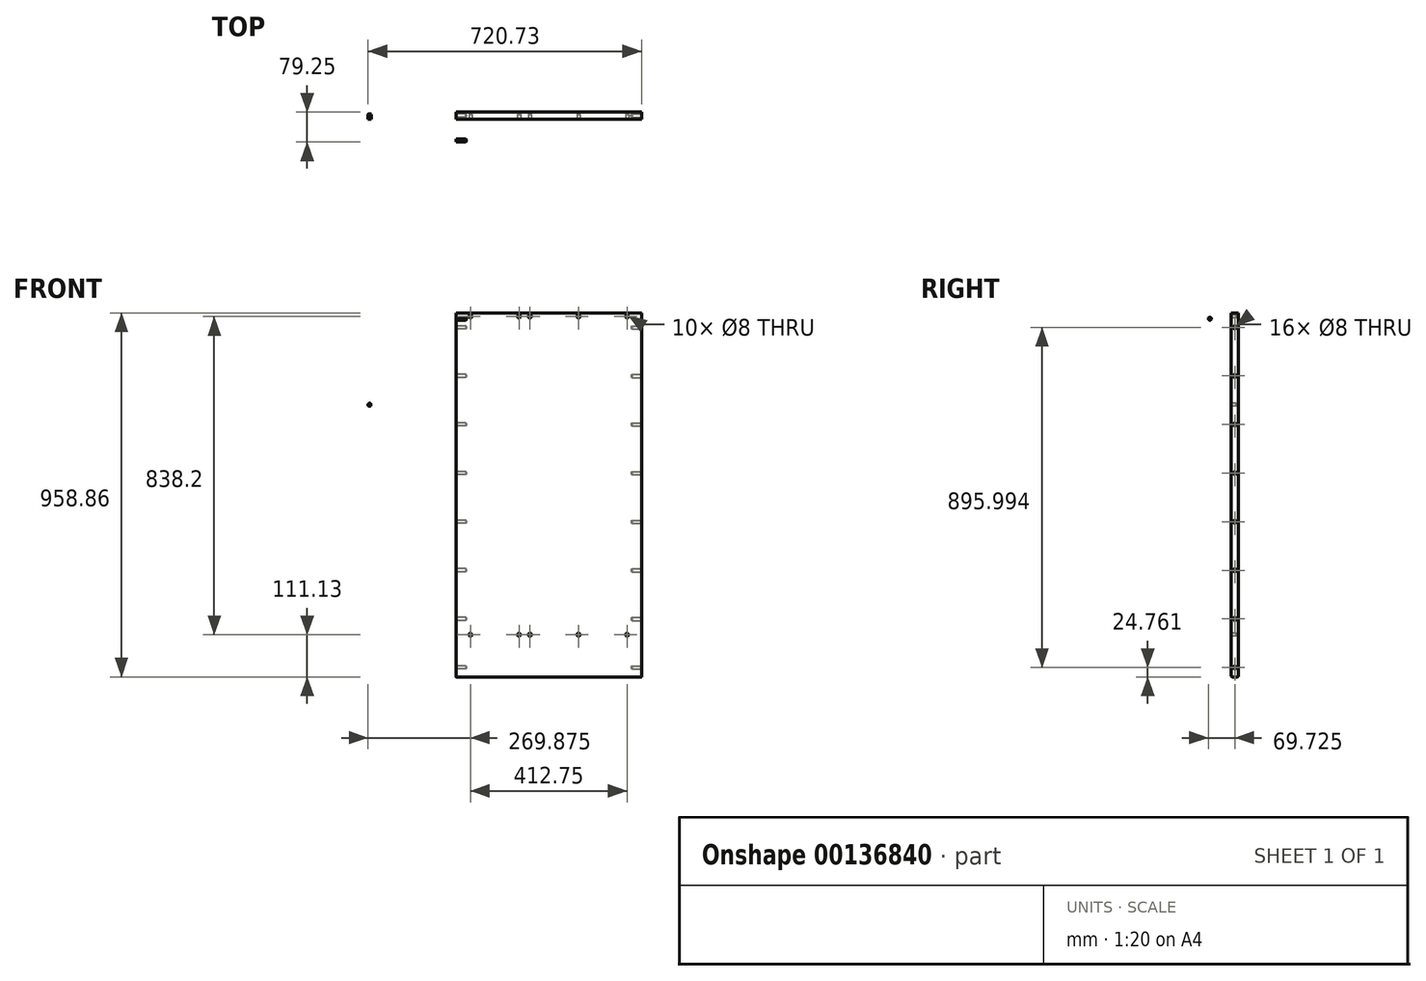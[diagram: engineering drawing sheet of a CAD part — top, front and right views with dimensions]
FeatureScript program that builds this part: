
annotation { "Feature Type Name" : "Feature", "Feature Type Description" : "" }
export const myFeature = defineFeature(function(context is Context, id is Id, definition is map)
    precondition{}
    {
        {
            var Q0;
            Q0=qCreatedBy(makeId("Front.planeOp"),FACE);
            var sketch = newSketch(context, id + "F0", { "sketchPlane" : qUnion([Q0])});
            skLineSegment(sketch, "E0.bottom", {"start": v(244.48, -479.43) * mm, "end": v(-244.47, -479.43) * mm});
            skLineSegment(sketch, "E0.top", {"start": v(244.47, 479.43) * mm, "end": v(-244.48, 479.43) * mm});
            skLineSegment(sketch, "E0.left", {"start": v(244.48, -479.43) * mm, "end": v(244.47, 479.42) * mm});
            skLineSegment(sketch, "E0.right", {"start": v(-244.47, -479.43) * mm, "end": v(-244.48, 479.43) * mm});
            skSolve(sketch);
        }
        {
            var Q0;
            Q0=makeQuery(id+"F0.imprint","IMPRINT",FACE,{"disambiguationData":[TD([[makeQuery(id+"F0.imprint","IMPRINT",EDGE,{"derivedFrom":sQuery(id+"F0.wireOp",EDGE,"E0.bottom")}),-1.0]])]});
            extrude(context, id + "F1", {"entities" : qUnion([Q0]), "oppositeDirection" : true, "depth" : 19.05 * mm});
        }
        {
            var Q0;
            Q0=makeQuery(id+"F1.opExtrude","SWEPT_FACE",FACE,{"disambiguationData":[OSD([sQuery(id+"F0.wireOp",EDGE,"E0.right")])]});
            var sketch = newSketch(context, id + "F2", { "sketchPlane" : qUnion([Q0])});
            skPoint(sketch, "E1", {"position": v(-9.53, 441.32) * mm});
            skPoint(sketch, "E2", {"position": v(-9.53, 313.32) * mm});
            skPoint(sketch, "E3", {"position": v(-9.52, 185.33) * mm});
            skPoint(sketch, "E4", {"position": v(-9.52, 57.33) * mm});
            skPoint(sketch, "E5", {"position": v(-9.52, -70.67) * mm});
            skPoint(sketch, "E6", {"position": v(-9.52, -198.67) * mm});
            skPoint(sketch, "E7", {"position": v(-9.52, -326.67) * mm});
            skPoint(sketch, "E8", {"position": v(-9.52, -454.67) * mm});
            skSolve(sketch);
        }
        {
            var Q0;
            {var subQ0=sQuery(id+"F0.wireOp",EDGE,"E0.right");Q0=makeQuery(id+"F2.imprint","IMPRINT",FACE,{"disambiguationData":[TD([[makeQuery(id+"F2.imprint","IMPRINT",EDGE,{"derivedFrom":makeQuery(id+"F1.opExtrude","CAP_EDGE",EDGE,{"disambiguationData":[OSD([subQ0])],"isStart":true})}),1.0]])]});}
            var sketch = newSketch(context, id + "F3", { "sketchPlane" : qUnion([Q0])});
            skCircle(sketch, "E9", {"center": v(56.2, 464.17) * mm, "radius": 4 * mm});
            skSolve(sketch);
        }
        {
            var Q0;
            Q0=makeQuery(id+"F3.imprint","IMPRINT",FACE,{"disambiguationData":[TD([[makeQuery(id+"F3.imprint","IMPRINT",EDGE,{"derivedFrom":sQuery(id+"F3.wireOp",EDGE,"E9")}),1.0]])]});
            var Q1;
            Q1=sQuery(id+"F3.wireOp",EDGE,"E9");
            extrude(context, id + "F31", {"entities" : qUnion([Q0]), "surfaceEntities" : qUnion([Q1]), "oppositeDirection" : true, "depth" : 26.99 * mm});
        }
        {
            var Q0;
            Q0=makeQuery(id+"F31.opExtrude","CAP_EDGE",EDGE,{"disambiguationData":[OSD([sQuery(id+"F3.wireOp",EDGE,"E9")])],"isStart":false});
            chamfer(context, id + "F4", {"entities" : qUnion([Q0]), "width" : 1.59 * mm, "tangentPropagation" : true});
        }
        {
            var Q0;
            Q0=makeQuery(id+"F31.opExtrude","CAP_FACE",FACE,{"disambiguationData":[OSD([sQuery(id+"F3.wireOp",EDGE,"E9")])],"isStart":true});
            var sketch = newSketch(context, id + "F5", { "sketchPlane" : qUnion([Q0])});
            skPoint(sketch, "E10", {"position": v(56.2, 464.17) * mm});
            skSolve(sketch);
        }
        {
            var Q0;
            Q0=makeQuery(id+"F31.opExtrude","SWEPT_BODY",BODY,{"disambiguationData":[OSD([sQuery(id+"F3.wireOp",EDGE,"E9")])]});
            var Q1;
            Q1=sQuery(id+"F5.wireOp",VERTEX,"E10");
            var Q2;
            Q2=sQuery(id+"F2.wireOp",VERTEX,"E1");
            transform(context, id + "F6", {"entities" : qUnion([Q0]), "transformType" : TransformType.TRANSLATION_ENTITY, "oppositeDirectionEntity" : false, "transformLine" : qUnion([Q1, Q2]), "makeCopy" : true});
        }
        {
            var Q0;
            Q0=makeQuery(id+"F6.opPattern","COPY",BODY,{"derivedFrom":makeQuery(id+"F31.opExtrude","SWEPT_BODY",BODY,{"disambiguationData":[OSD([sQuery(id+"F3.wireOp",EDGE,"E9")])]}),"instanceName":"1"});
            var Q1;
            Q1=sQuery(id+"F2.wireOp",VERTEX,"E1");
            var Q2;
            Q2=sQuery(id+"F2.wireOp",VERTEX,"E2");
            transform(context, id + "F7", {"entities" : qUnion([Q0]), "transformType" : TransformType.TRANSLATION_ENTITY, "oppositeDirectionEntity" : false, "transformLine" : qUnion([Q1, Q2]), "makeCopy" : true});
        }
        {
            var Q0;
            Q0=makeQuery(id+"F7.opPattern","COPY",BODY,{"derivedFrom":makeQuery(id+"F6.opPattern","COPY",BODY,{"derivedFrom":makeQuery(id+"F31.opExtrude","SWEPT_BODY",BODY,{"disambiguationData":[OSD([sQuery(id+"F3.wireOp",EDGE,"E9")])]}),"instanceName":"1"}),"instanceName":"1"});
            var Q1;
            Q1=sQuery(id+"F2.wireOp",VERTEX,"E2");
            var Q2;
            Q2=sQuery(id+"F2.wireOp",VERTEX,"E3");
            transform(context, id + "F32", {"entities" : qUnion([Q0]), "transformType" : TransformType.TRANSLATION_ENTITY, "oppositeDirectionEntity" : false, "transformLine" : qUnion([Q1, Q2]), "makeCopy" : true});
        }
        {
            var Q0;
            Q0=makeQuery(id+"F31.opExtrude","SWEPT_BODY",BODY,{"disambiguationData":[OSD([sQuery(id+"F3.wireOp",EDGE,"E9")])]});
            var Q1;
            Q1=sQuery(id+"F5.wireOp",VERTEX,"E10");
            var Q2;
            Q2=sQuery(id+"F2.wireOp",VERTEX,"E4");
            transform(context, id + "F8", {"entities" : qUnion([Q0]), "transformType" : TransformType.TRANSLATION_ENTITY, "oppositeDirectionEntity" : false, "transformLine" : qUnion([Q1, Q2]), "makeCopy" : true});
        }
        {
            var Q0;
            Q0=makeQuery(id+"F31.opExtrude","SWEPT_BODY",BODY,{"disambiguationData":[OSD([sQuery(id+"F3.wireOp",EDGE,"E9")])]});
            var Q1;
            Q1=sQuery(id+"F5.wireOp",VERTEX,"E10");
            var Q2;
            Q2=sQuery(id+"F2.wireOp",VERTEX,"E5");
            transform(context, id + "F9", {"entities" : qUnion([Q0]), "transformType" : TransformType.TRANSLATION_ENTITY, "oppositeDirectionEntity" : false, "transformLine" : qUnion([Q1, Q2]), "makeCopy" : true});
        }
        {
            var Q0;
            Q0=makeQuery(id+"F31.opExtrude","SWEPT_BODY",BODY,{"disambiguationData":[OSD([sQuery(id+"F3.wireOp",EDGE,"E9")])]});
            var Q1;
            Q1=sQuery(id+"F5.wireOp",VERTEX,"E10");
            var Q2;
            Q2=sQuery(id+"F2.wireOp",VERTEX,"E6");
            transform(context, id + "F10", {"entities" : qUnion([Q0]), "transformType" : TransformType.TRANSLATION_ENTITY, "oppositeDirectionEntity" : false, "transformLine" : qUnion([Q1, Q2]), "makeCopy" : true});
        }
        {
            var Q0;
            Q0=makeQuery(id+"F31.opExtrude","SWEPT_BODY",BODY,{"disambiguationData":[OSD([sQuery(id+"F3.wireOp",EDGE,"E9")])]});
            var Q1;
            Q1=sQuery(id+"F5.wireOp",VERTEX,"E10");
            var Q2;
            Q2=sQuery(id+"F2.wireOp",VERTEX,"E7");
            transform(context, id + "F11", {"entities" : qUnion([Q0]), "transformType" : TransformType.TRANSLATION_ENTITY, "oppositeDirectionEntity" : false, "transformLine" : qUnion([Q1, Q2]), "makeCopy" : true});
        }
        {
            var Q0;
            Q0=makeQuery(id+"F31.opExtrude","SWEPT_BODY",BODY,{"disambiguationData":[OSD([sQuery(id+"F3.wireOp",EDGE,"E9")])]});
            var Q1;
            Q1=sQuery(id+"F5.wireOp",VERTEX,"E10");
            var Q2;
            Q2=sQuery(id+"F2.wireOp",VERTEX,"E8");
            transform(context, id + "F12", {"entities" : qUnion([Q0]), "transformType" : TransformType.TRANSLATION_ENTITY, "oppositeDirectionEntity" : false, "transformLine" : qUnion([Q1, Q2]), "makeCopy" : true});
        }
        {
            var Q0;
            Q0=makeQuery(id+"F6.opPattern","COPY",BODY,{"derivedFrom":makeQuery(id+"F31.opExtrude","SWEPT_BODY",BODY,{"disambiguationData":[OSD([sQuery(id+"F3.wireOp",EDGE,"E9")])]}),"instanceName":"1"});
            var Q1;
            Q1=makeQuery(id+"F7.opPattern","COPY",BODY,{"derivedFrom":makeQuery(id+"F6.opPattern","COPY",BODY,{"derivedFrom":makeQuery(id+"F31.opExtrude","SWEPT_BODY",BODY,{"disambiguationData":[OSD([sQuery(id+"F3.wireOp",EDGE,"E9")])]}),"instanceName":"1"}),"instanceName":"1"});
            var Q2;
            Q2=makeQuery(id+"F32.opPattern","COPY",BODY,{"derivedFrom":makeQuery(id+"F7.opPattern","COPY",BODY,{"derivedFrom":makeQuery(id+"F6.opPattern","COPY",BODY,{"derivedFrom":makeQuery(id+"F31.opExtrude","SWEPT_BODY",BODY,{"disambiguationData":[OSD([sQuery(id+"F3.wireOp",EDGE,"E9")])]}),"instanceName":"1"}),"instanceName":"1"}),"instanceName":"1"});
            var Q3;
            Q3=makeQuery(id+"F8.opPattern","COPY",BODY,{"derivedFrom":makeQuery(id+"F31.opExtrude","SWEPT_BODY",BODY,{"disambiguationData":[OSD([sQuery(id+"F3.wireOp",EDGE,"E9")])]}),"instanceName":"1"});
            var Q4;
            Q4=makeQuery(id+"F9.opPattern","COPY",BODY,{"derivedFrom":makeQuery(id+"F31.opExtrude","SWEPT_BODY",BODY,{"disambiguationData":[OSD([sQuery(id+"F3.wireOp",EDGE,"E9")])]}),"instanceName":"1"});
            var Q5;
            Q5=makeQuery(id+"F10.opPattern","COPY",BODY,{"derivedFrom":makeQuery(id+"F31.opExtrude","SWEPT_BODY",BODY,{"disambiguationData":[OSD([sQuery(id+"F3.wireOp",EDGE,"E9")])]}),"instanceName":"1"});
            var Q6;
            Q6=makeQuery(id+"F11.opPattern","COPY",BODY,{"derivedFrom":makeQuery(id+"F31.opExtrude","SWEPT_BODY",BODY,{"disambiguationData":[OSD([sQuery(id+"F3.wireOp",EDGE,"E9")])]}),"instanceName":"1"});
            var Q7;
            Q7=makeQuery(id+"F12.opPattern","COPY",BODY,{"derivedFrom":makeQuery(id+"F31.opExtrude","SWEPT_BODY",BODY,{"disambiguationData":[OSD([sQuery(id+"F3.wireOp",EDGE,"E9")])]}),"instanceName":"1"});
            var Q8;
            Q8=qCreatedBy(makeId("Right.planeOp"),FACE);
            mirror(context, id + "F13", {"entities" : qUnion([Q0, Q1, Q2, Q3, Q4, Q5, Q6, Q7]), "mirrorPlane" : qUnion([Q8])});
        }
        {
            var Q0;
            Q0=makeQuery(id+"F13.opPattern","COPY",BODY,{"derivedFrom":makeQuery(id+"F6.opPattern","COPY",BODY,{"derivedFrom":makeQuery(id+"F31.opExtrude","SWEPT_BODY",BODY,{"disambiguationData":[OSD([sQuery(id+"F3.wireOp",EDGE,"E9")])]}),"instanceName":"1"}),"instanceName":"1"});
            var Q1;
            Q1=makeQuery(id+"F13.opPattern","COPY",BODY,{"derivedFrom":makeQuery(id+"F7.opPattern","COPY",BODY,{"derivedFrom":makeQuery(id+"F6.opPattern","COPY",BODY,{"derivedFrom":makeQuery(id+"F31.opExtrude","SWEPT_BODY",BODY,{"disambiguationData":[OSD([sQuery(id+"F3.wireOp",EDGE,"E9")])]}),"instanceName":"1"}),"instanceName":"1"}),"instanceName":"1"});
            var Q2;
            Q2=makeQuery(id+"F13.opPattern","COPY",BODY,{"derivedFrom":makeQuery(id+"F32.opPattern","COPY",BODY,{"derivedFrom":makeQuery(id+"F7.opPattern","COPY",BODY,{"derivedFrom":makeQuery(id+"F6.opPattern","COPY",BODY,{"derivedFrom":makeQuery(id+"F31.opExtrude","SWEPT_BODY",BODY,{"disambiguationData":[OSD([sQuery(id+"F3.wireOp",EDGE,"E9")])]}),"instanceName":"1"}),"instanceName":"1"}),"instanceName":"1"}),"instanceName":"1"});
            var Q3;
            Q3=makeQuery(id+"F13.opPattern","COPY",BODY,{"derivedFrom":makeQuery(id+"F8.opPattern","COPY",BODY,{"derivedFrom":makeQuery(id+"F31.opExtrude","SWEPT_BODY",BODY,{"disambiguationData":[OSD([sQuery(id+"F3.wireOp",EDGE,"E9")])]}),"instanceName":"1"}),"instanceName":"1"});
            var Q4;
            Q4=makeQuery(id+"F13.opPattern","COPY",BODY,{"derivedFrom":makeQuery(id+"F9.opPattern","COPY",BODY,{"derivedFrom":makeQuery(id+"F31.opExtrude","SWEPT_BODY",BODY,{"disambiguationData":[OSD([sQuery(id+"F3.wireOp",EDGE,"E9")])]}),"instanceName":"1"}),"instanceName":"1"});
            var Q5;
            Q5=makeQuery(id+"F13.opPattern","COPY",BODY,{"derivedFrom":makeQuery(id+"F10.opPattern","COPY",BODY,{"derivedFrom":makeQuery(id+"F31.opExtrude","SWEPT_BODY",BODY,{"disambiguationData":[OSD([sQuery(id+"F3.wireOp",EDGE,"E9")])]}),"instanceName":"1"}),"instanceName":"1"});
            var Q6;
            Q6=makeQuery(id+"F13.opPattern","COPY",BODY,{"derivedFrom":makeQuery(id+"F11.opPattern","COPY",BODY,{"derivedFrom":makeQuery(id+"F31.opExtrude","SWEPT_BODY",BODY,{"disambiguationData":[OSD([sQuery(id+"F3.wireOp",EDGE,"E9")])]}),"instanceName":"1"}),"instanceName":"1"});
            var Q7;
            Q7=makeQuery(id+"F13.opPattern","COPY",BODY,{"derivedFrom":makeQuery(id+"F12.opPattern","COPY",BODY,{"derivedFrom":makeQuery(id+"F31.opExtrude","SWEPT_BODY",BODY,{"disambiguationData":[OSD([sQuery(id+"F3.wireOp",EDGE,"E9")])]}),"instanceName":"1"}),"instanceName":"1"});
            var Q8;
            Q8=makeQuery(id+"F6.opPattern","COPY",BODY,{"derivedFrom":makeQuery(id+"F31.opExtrude","SWEPT_BODY",BODY,{"disambiguationData":[OSD([sQuery(id+"F3.wireOp",EDGE,"E9")])]}),"instanceName":"1"});
            var Q9;
            Q9=makeQuery(id+"F7.opPattern","COPY",BODY,{"derivedFrom":makeQuery(id+"F6.opPattern","COPY",BODY,{"derivedFrom":makeQuery(id+"F31.opExtrude","SWEPT_BODY",BODY,{"disambiguationData":[OSD([sQuery(id+"F3.wireOp",EDGE,"E9")])]}),"instanceName":"1"}),"instanceName":"1"});
            var Q10;
            Q10=makeQuery(id+"F32.opPattern","COPY",BODY,{"derivedFrom":makeQuery(id+"F7.opPattern","COPY",BODY,{"derivedFrom":makeQuery(id+"F6.opPattern","COPY",BODY,{"derivedFrom":makeQuery(id+"F31.opExtrude","SWEPT_BODY",BODY,{"disambiguationData":[OSD([sQuery(id+"F3.wireOp",EDGE,"E9")])]}),"instanceName":"1"}),"instanceName":"1"}),"instanceName":"1"});
            var Q11;
            Q11=makeQuery(id+"F8.opPattern","COPY",BODY,{"derivedFrom":makeQuery(id+"F31.opExtrude","SWEPT_BODY",BODY,{"disambiguationData":[OSD([sQuery(id+"F3.wireOp",EDGE,"E9")])]}),"instanceName":"1"});
            var Q12;
            Q12=makeQuery(id+"F9.opPattern","COPY",BODY,{"derivedFrom":makeQuery(id+"F31.opExtrude","SWEPT_BODY",BODY,{"disambiguationData":[OSD([sQuery(id+"F3.wireOp",EDGE,"E9")])]}),"instanceName":"1"});
            var Q13;
            Q13=makeQuery(id+"F10.opPattern","COPY",BODY,{"derivedFrom":makeQuery(id+"F31.opExtrude","SWEPT_BODY",BODY,{"disambiguationData":[OSD([sQuery(id+"F3.wireOp",EDGE,"E9")])]}),"instanceName":"1"});
            var Q14;
            Q14=makeQuery(id+"F11.opPattern","COPY",BODY,{"derivedFrom":makeQuery(id+"F31.opExtrude","SWEPT_BODY",BODY,{"disambiguationData":[OSD([sQuery(id+"F3.wireOp",EDGE,"E9")])]}),"instanceName":"1"});
            var Q15;
            Q15=makeQuery(id+"F12.opPattern","COPY",BODY,{"derivedFrom":makeQuery(id+"F31.opExtrude","SWEPT_BODY",BODY,{"disambiguationData":[OSD([sQuery(id+"F3.wireOp",EDGE,"E9")])]}),"instanceName":"1"});
            var Q16;
            Q16=makeQuery(id+"F1.opExtrude","SWEPT_BODY",BODY,{"disambiguationData":[OSD([sQuery(id+"F0.wireOp",EDGE,"E0.bottom"),sQuery(id+"F0.wireOp",EDGE,"E0.top"),sQuery(id+"F0.wireOp",EDGE,"E0.left"),sQuery(id+"F0.wireOp",EDGE,"E0.right")])]});
            booleanBodies(context, id + "F14", {"operationType" : BooleanOperationType.SUBTRACTION, "tools" : qUnion([Q0, Q1, Q2, Q3, Q4, Q5, Q6, Q7, Q8, Q9, Q10, Q11, Q12, Q13, Q14, Q15]), "targets" : qUnion([Q16])});
        }
        {
            var Q0;
            Q0=makeQuery(id+"F0.imprint","IMPRINT",FACE,{"disambiguationData":[TD([[makeQuery(id+"F0.imprint","IMPRINT",EDGE,{"derivedFrom":sQuery(id+"F0.wireOp",EDGE,"E0.bottom")}),-1.0]])]});
            var sketch = newSketch(context, id + "F15", { "sketchPlane" : qUnion([Q0])});
            skPoint(sketch, "E11", {"position": v(-206.38, 469.9) * mm});
            skPoint(sketch, "E12", {"position": v(-78.38, 469.9) * mm});
            skPoint(sketch, "E13", {"position": v(-49.62, 469.9) * mm});
            skPoint(sketch, "E14", {"position": v(78.38, 469.9) * mm});
            skPoint(sketch, "E15", {"position": v(206.37, 469.9) * mm});
            skPoint(sketch, "E16", {"position": v(-206.38, -368.3) * mm});
            skPoint(sketch, "E17", {"position": v(-78.38, -368.3) * mm});
            skPoint(sketch, "E18", {"position": v(-49.62, -368.3) * mm});
            skPoint(sketch, "E19", {"position": v(78.38, -368.3) * mm});
            skPoint(sketch, "E20", {"position": v(206.37, -368.3) * mm});
            skSolve(sketch);
        }
        {
            var Q0;
            Q0=qCreatedBy(makeId("Front.planeOp"),FACE);
            var sketch = newSketch(context, id + "F16", { "sketchPlane" : qUnion([Q0])});
            skPoint(sketch, "E21", {"position": v(-472.25, 237.26) * mm});
            skCircle(sketch, "E22", {"center": v(-472.25, 237.26) * mm, "radius": 4 * mm});
            skSolve(sketch);
        }
        {
            var Q0;
            Q0=makeQuery(id+"F16.imprint","IMPRINT",FACE,{"disambiguationData":[TD([[makeQuery(id+"F16.imprint","IMPRINT",EDGE,{"derivedFrom":sQuery(id+"F16.wireOp",EDGE,"E22")}),1.0]])]});
            extrude(context, id + "F17", {"entities" : qUnion([Q0]), "oppositeDirection" : true, "depth" : 14.29 * mm});
        }
        {
            var Q0;
            Q0=makeQuery(id+"F17.opExtrude","CAP_EDGE",EDGE,{"disambiguationData":[OSD([sQuery(id+"F16.wireOp",EDGE,"E22")])],"isStart":false});
            chamfer(context, id + "F18", {"entities" : qUnion([Q0]), "width" : 1.59 * mm, "tangentPropagation" : true});
        }
        {
            var Q0;
            Q0=makeQuery(id+"F17.opExtrude","SWEPT_BODY",BODY,{"disambiguationData":[OSD([sQuery(id+"F16.wireOp",EDGE,"E22")])]});
            var Q1;
            Q1=sQuery(id+"F16.wireOp",VERTEX,"E21");
            var Q2;
            Q2=sQuery(id+"F15.wireOp",VERTEX,"E11");
            transform(context, id + "F19", {"entities" : qUnion([Q0]), "transformType" : TransformType.TRANSLATION_ENTITY, "oppositeDirectionEntity" : false, "transformLine" : qUnion([Q1, Q2]), "makeCopy" : true});
        }
        {
            var Q0;
            Q0=makeQuery(id+"F17.opExtrude","SWEPT_BODY",BODY,{"disambiguationData":[OSD([sQuery(id+"F16.wireOp",EDGE,"E22")])]});
            var Q1;
            Q1=sQuery(id+"F16.wireOp",VERTEX,"E21");
            var Q2;
            Q2=sQuery(id+"F15.wireOp",VERTEX,"E12");
            transform(context, id + "F20", {"entities" : qUnion([Q0]), "transformType" : TransformType.TRANSLATION_ENTITY, "oppositeDirectionEntity" : false, "transformLine" : qUnion([Q1, Q2]), "makeCopy" : true});
        }
        {
            var Q0;
            Q0=makeQuery(id+"F17.opExtrude","SWEPT_BODY",BODY,{"disambiguationData":[OSD([sQuery(id+"F16.wireOp",EDGE,"E22")])]});
            var Q1;
            Q1=sQuery(id+"F16.wireOp",VERTEX,"E21");
            var Q2;
            Q2=sQuery(id+"F15.wireOp",VERTEX,"E13");
            transform(context, id + "F21", {"entities" : qUnion([Q0]), "transformType" : TransformType.TRANSLATION_ENTITY, "oppositeDirectionEntity" : false, "transformLine" : qUnion([Q1, Q2]), "makeCopy" : true});
        }
        {
            var Q0;
            Q0=makeQuery(id+"F17.opExtrude","SWEPT_BODY",BODY,{"disambiguationData":[OSD([sQuery(id+"F16.wireOp",EDGE,"E22")])]});
            var Q1;
            Q1=sQuery(id+"F16.wireOp",VERTEX,"E21");
            var Q2;
            Q2=sQuery(id+"F15.wireOp",VERTEX,"E14");
            transform(context, id + "F22", {"entities" : qUnion([Q0]), "transformType" : TransformType.TRANSLATION_ENTITY, "oppositeDirectionEntity" : false, "transformLine" : qUnion([Q1, Q2]), "makeCopy" : true});
        }
        {
            var Q0;
            Q0=makeQuery(id+"F17.opExtrude","SWEPT_BODY",BODY,{"disambiguationData":[OSD([sQuery(id+"F16.wireOp",EDGE,"E22")])]});
            var Q1;
            Q1=sQuery(id+"F16.wireOp",VERTEX,"E21");
            var Q2;
            Q2=sQuery(id+"F15.wireOp",VERTEX,"E15");
            transform(context, id + "F23", {"entities" : qUnion([Q0]), "transformType" : TransformType.TRANSLATION_ENTITY, "oppositeDirectionEntity" : false, "transformLine" : qUnion([Q1, Q2]), "makeCopy" : true});
        }
        {
            var Q0;
            Q0=makeQuery(id+"F17.opExtrude","SWEPT_BODY",BODY,{"disambiguationData":[OSD([sQuery(id+"F16.wireOp",EDGE,"E22")])]});
            var Q1;
            Q1=sQuery(id+"F16.wireOp",VERTEX,"E21");
            var Q2;
            Q2=sQuery(id+"F15.wireOp",VERTEX,"E16");
            transform(context, id + "F24", {"entities" : qUnion([Q0]), "transformType" : TransformType.TRANSLATION_ENTITY, "oppositeDirectionEntity" : false, "transformLine" : qUnion([Q1, Q2]), "makeCopy" : true});
        }
        {
            var Q0;
            Q0=makeQuery(id+"F17.opExtrude","SWEPT_BODY",BODY,{"disambiguationData":[OSD([sQuery(id+"F16.wireOp",EDGE,"E22")])]});
            var Q1;
            Q1=sQuery(id+"F16.wireOp",VERTEX,"E21");
            var Q2;
            Q2=sQuery(id+"F15.wireOp",VERTEX,"E17");
            transform(context, id + "F25", {"entities" : qUnion([Q0]), "transformType" : TransformType.TRANSLATION_ENTITY, "oppositeDirectionEntity" : false, "transformLine" : qUnion([Q1, Q2]), "makeCopy" : true});
        }
        {
            var Q0;
            Q0=makeQuery(id+"F17.opExtrude","SWEPT_BODY",BODY,{"disambiguationData":[OSD([sQuery(id+"F16.wireOp",EDGE,"E22")])]});
            var Q1;
            Q1=sQuery(id+"F16.wireOp",VERTEX,"E21");
            var Q2;
            Q2=sQuery(id+"F15.wireOp",VERTEX,"E18");
            transform(context, id + "F26", {"entities" : qUnion([Q0]), "transformType" : TransformType.TRANSLATION_ENTITY, "oppositeDirectionEntity" : false, "transformLine" : qUnion([Q1, Q2]), "makeCopy" : true});
        }
        {
            var Q0;
            Q0=makeQuery(id+"F17.opExtrude","SWEPT_BODY",BODY,{"disambiguationData":[OSD([sQuery(id+"F16.wireOp",EDGE,"E22")])]});
            var Q1;
            Q1=sQuery(id+"F16.wireOp",VERTEX,"E21");
            var Q2;
            Q2=sQuery(id+"F15.wireOp",VERTEX,"E19");
            transform(context, id + "F27", {"entities" : qUnion([Q0]), "transformType" : TransformType.TRANSLATION_ENTITY, "oppositeDirectionEntity" : false, "transformLine" : qUnion([Q1, Q2]), "makeCopy" : true});
        }
        {
            var Q0;
            Q0=makeQuery(id+"F17.opExtrude","SWEPT_BODY",BODY,{"disambiguationData":[OSD([sQuery(id+"F16.wireOp",EDGE,"E22")])]});
            var Q1;
            Q1=sQuery(id+"F16.wireOp",VERTEX,"E21");
            var Q2;
            Q2=sQuery(id+"F15.wireOp",VERTEX,"E20");
            transform(context, id + "F28", {"entities" : qUnion([Q0]), "transformType" : TransformType.TRANSLATION_ENTITY, "oppositeDirectionEntity" : false, "transformLine" : qUnion([Q1, Q2]), "makeCopy" : true});
        }
        {
            var Q0;
            Q0=makeQuery(id+"F24.opPattern","COPY",BODY,{"derivedFrom":makeQuery(id+"F17.opExtrude","SWEPT_BODY",BODY,{"disambiguationData":[OSD([sQuery(id+"F16.wireOp",EDGE,"E22")])]}),"instanceName":"1"});
            var Q1;
            Q1=makeQuery(id+"F25.opPattern","COPY",BODY,{"derivedFrom":makeQuery(id+"F17.opExtrude","SWEPT_BODY",BODY,{"disambiguationData":[OSD([sQuery(id+"F16.wireOp",EDGE,"E22")])]}),"instanceName":"1"});
            var Q2;
            Q2=makeQuery(id+"F26.opPattern","COPY",BODY,{"derivedFrom":makeQuery(id+"F17.opExtrude","SWEPT_BODY",BODY,{"disambiguationData":[OSD([sQuery(id+"F16.wireOp",EDGE,"E22")])]}),"instanceName":"1"});
            var Q3;
            Q3=makeQuery(id+"F27.opPattern","COPY",BODY,{"derivedFrom":makeQuery(id+"F17.opExtrude","SWEPT_BODY",BODY,{"disambiguationData":[OSD([sQuery(id+"F16.wireOp",EDGE,"E22")])]}),"instanceName":"1"});
            var Q4;
            Q4=makeQuery(id+"F28.opPattern","COPY",BODY,{"derivedFrom":makeQuery(id+"F17.opExtrude","SWEPT_BODY",BODY,{"disambiguationData":[OSD([sQuery(id+"F16.wireOp",EDGE,"E22")])]}),"instanceName":"1"});
            var Q5;
            Q5=makeQuery(id+"F19.opPattern","COPY",BODY,{"derivedFrom":makeQuery(id+"F17.opExtrude","SWEPT_BODY",BODY,{"disambiguationData":[OSD([sQuery(id+"F16.wireOp",EDGE,"E22")])]}),"instanceName":"1"});
            var Q6;
            Q6=makeQuery(id+"F20.opPattern","COPY",BODY,{"derivedFrom":makeQuery(id+"F17.opExtrude","SWEPT_BODY",BODY,{"disambiguationData":[OSD([sQuery(id+"F16.wireOp",EDGE,"E22")])]}),"instanceName":"1"});
            var Q7;
            Q7=makeQuery(id+"F21.opPattern","COPY",BODY,{"derivedFrom":makeQuery(id+"F17.opExtrude","SWEPT_BODY",BODY,{"disambiguationData":[OSD([sQuery(id+"F16.wireOp",EDGE,"E22")])]}),"instanceName":"1"});
            var Q8;
            Q8=makeQuery(id+"F22.opPattern","COPY",BODY,{"derivedFrom":makeQuery(id+"F17.opExtrude","SWEPT_BODY",BODY,{"disambiguationData":[OSD([sQuery(id+"F16.wireOp",EDGE,"E22")])]}),"instanceName":"1"});
            var Q9;
            Q9=makeQuery(id+"F23.opPattern","COPY",BODY,{"derivedFrom":makeQuery(id+"F17.opExtrude","SWEPT_BODY",BODY,{"disambiguationData":[OSD([sQuery(id+"F16.wireOp",EDGE,"E22")])]}),"instanceName":"1"});
            var Q10;
            Q10=makeQuery(id+"F1.opExtrude","SWEPT_BODY",BODY,{"disambiguationData":[OSD([sQuery(id+"F0.wireOp",EDGE,"E0.bottom"),sQuery(id+"F0.wireOp",EDGE,"E0.top"),sQuery(id+"F0.wireOp",EDGE,"E0.left"),sQuery(id+"F0.wireOp",EDGE,"E0.right")])]});
            booleanBodies(context, id + "F29", {"operationType" : BooleanOperationType.SUBTRACTION, "tools" : qUnion([Q0, Q1, Q2, Q3, Q4, Q5, Q6, Q7, Q8, Q9]), "targets" : qUnion([Q10])});
        }
        {
            var Q0;
            Q0=makeQuery(id+"F1.opExtrude","CAP_EDGE",EDGE,{"disambiguationData":[OSD([sQuery(id+"F0.wireOp",EDGE,"E0.bottom")])],"isStart":false});
            var Q1;
            Q1=makeQuery(id+"F1.opExtrude","CAP_EDGE",EDGE,{"disambiguationData":[OSD([sQuery(id+"F0.wireOp",EDGE,"E0.bottom")])],"isStart":true});
            fillet(context, id + "F30", {"entities" : qUnion([Q0, Q1]), "radius" : 3.17 * mm, "tangentPropagation" : true, "allowEdgeOverflow" : false});
        }
    });
